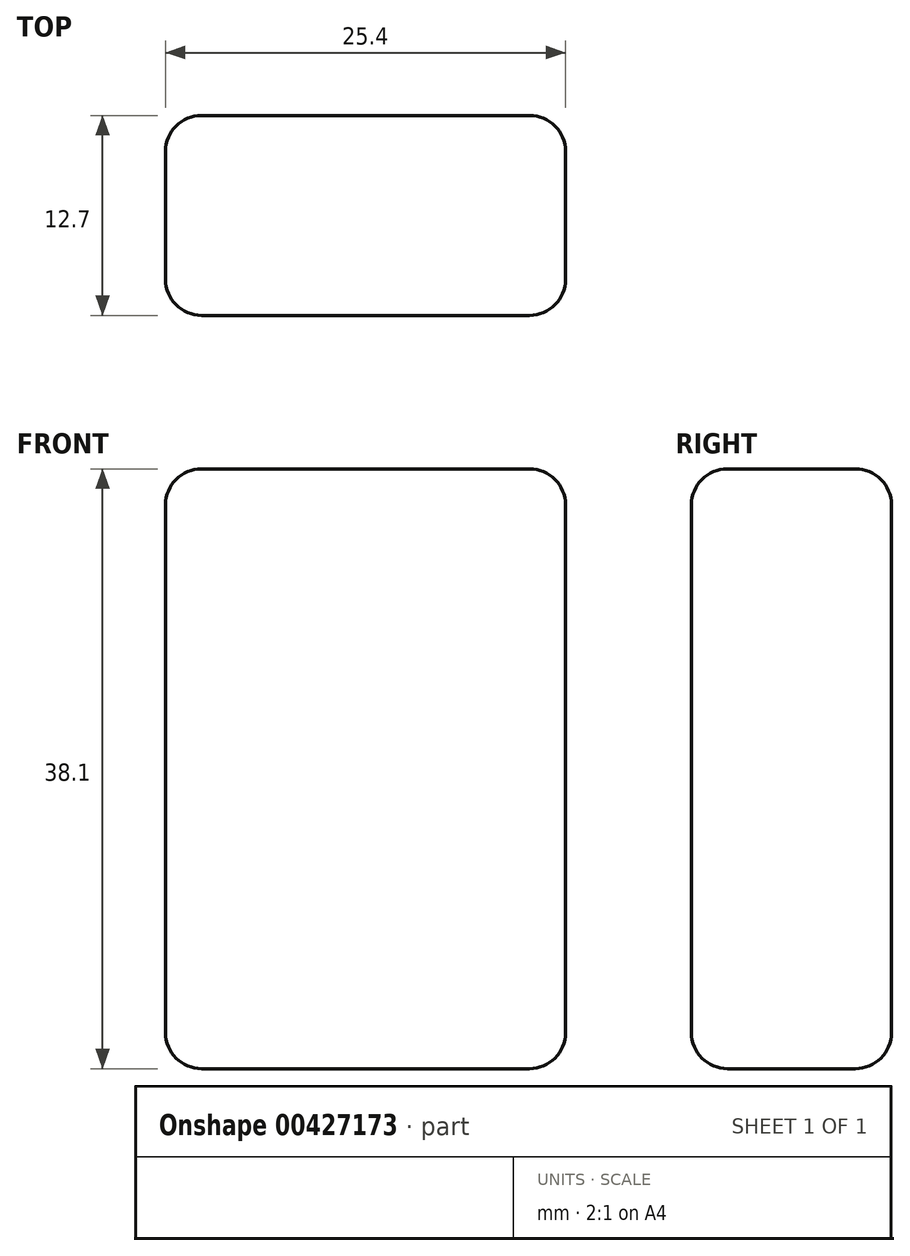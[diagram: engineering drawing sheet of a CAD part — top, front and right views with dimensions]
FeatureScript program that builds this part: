
annotation { "Feature Type Name" : "Feature", "Feature Type Description" : "" }
export const myFeature = defineFeature(function(context is Context, id is Id, definition is map)
    precondition{}
    {
        {
            var Q0;
            Q0=qCreatedBy(makeId("Top.planeOp"),FACE);
            var sketch = newSketch(context, id + "F0", { "sketchPlane" : qUnion([Q0])});
            skLineSegment(sketch, "E0.bottom", {"start": v(0, 0) * mm, "end": v(25.4, 0) * mm});
            skLineSegment(sketch, "E0.top", {"start": v(0, -12.7) * mm, "end": v(25.4, -12.7) * mm});
            skLineSegment(sketch, "E0.left", {"start": v(0, 0) * mm, "end": v(0, -12.7) * mm});
            skLineSegment(sketch, "E0.right", {"start": v(25.4, 0) * mm, "end": v(25.4, -12.7) * mm});
            skSolve(sketch);
        }
        {
            var Q0;
            Q0=makeQuery(id+"F0.imprint","IMPRINT",FACE,{"disambiguationData":[TD([[makeQuery(id+"F0.imprint","IMPRINT",EDGE,{"derivedFrom":sQuery(id+"F0.wireOp",EDGE,"E0.bottom")}),-1.0]])]});
            extrude(context, id + "F1", {"entities" : qUnion([Q0]), "depth" : 38.1 * mm});
        }
        {
            var Q0;
            Q0=makeQuery(id+"F1.opExtrude","SWEPT_EDGE",EDGE,{"disambiguationData":[OSD([sQuery(id+"F0.wireOp",EDGE,"E0.top"),sQuery(id+"F0.wireOp",EDGE,"E0.right")])]});
            var Q1;
            Q1=makeQuery(id+"F1.opExtrude","SWEPT_EDGE",EDGE,{"disambiguationData":[OSD([sQuery(id+"F0.wireOp",EDGE,"E0.top"),sQuery(id+"F0.wireOp",EDGE,"E0.left")])]});
            var Q2;
            Q2=makeQuery(id+"F1.opExtrude","SWEPT_EDGE",EDGE,{"disambiguationData":[OSD([sQuery(id+"F0.wireOp",EDGE,"E0.bottom"),sQuery(id+"F0.wireOp",EDGE,"E0.right")])]});
            var Q3;
            Q3=makeQuery(id+"F1.opExtrude","SWEPT_EDGE",EDGE,{"disambiguationData":[OSD([sQuery(id+"F0.wireOp",EDGE,"E0.bottom"),sQuery(id+"F0.wireOp",EDGE,"E0.left")])]});
            var Q4;
            Q4=makeQuery(id+"F1.opExtrude","CAP_EDGE",EDGE,{"disambiguationData":[OSD([sQuery(id+"F0.wireOp",EDGE,"E0.bottom")])],"isStart":false});
            var Q5;
            Q5=makeQuery(id+"F1.opExtrude","CAP_EDGE",EDGE,{"disambiguationData":[OSD([sQuery(id+"F0.wireOp",EDGE,"E0.right")])],"isStart":false});
            var Q6;
            Q6=makeQuery(id+"F1.opExtrude","CAP_EDGE",EDGE,{"disambiguationData":[OSD([sQuery(id+"F0.wireOp",EDGE,"E0.top")])],"isStart":false});
            var Q7;
            Q7=makeQuery(id+"F1.opExtrude","CAP_EDGE",EDGE,{"disambiguationData":[OSD([sQuery(id+"F0.wireOp",EDGE,"E0.left")])],"isStart":false});
            var Q8;
            Q8=makeQuery(id+"F1.opExtrude","CAP_EDGE",EDGE,{"disambiguationData":[OSD([sQuery(id+"F0.wireOp",EDGE,"E0.right")])],"isStart":true});
            var Q9;
            Q9=makeQuery(id+"F1.opExtrude","CAP_EDGE",EDGE,{"disambiguationData":[OSD([sQuery(id+"F0.wireOp",EDGE,"E0.top")])],"isStart":true});
            var Q10;
            Q10=makeQuery(id+"F1.opExtrude","CAP_EDGE",EDGE,{"disambiguationData":[OSD([sQuery(id+"F0.wireOp",EDGE,"E0.bottom")])],"isStart":true});
            var Q11;
            Q11=makeQuery(id+"F1.opExtrude","CAP_EDGE",EDGE,{"disambiguationData":[OSD([sQuery(id+"F0.wireOp",EDGE,"E0.left")])],"isStart":true});
            fillet(context, id + "F2", {"entities" : qUnion([Q0, Q1, Q2, Q3, Q4, Q5, Q6, Q7, Q8, Q9, Q10, Q11]), "radius" : 2.3 * mm, "tangentPropagation" : true, "allowEdgeOverflow" : false});
        }
    });
